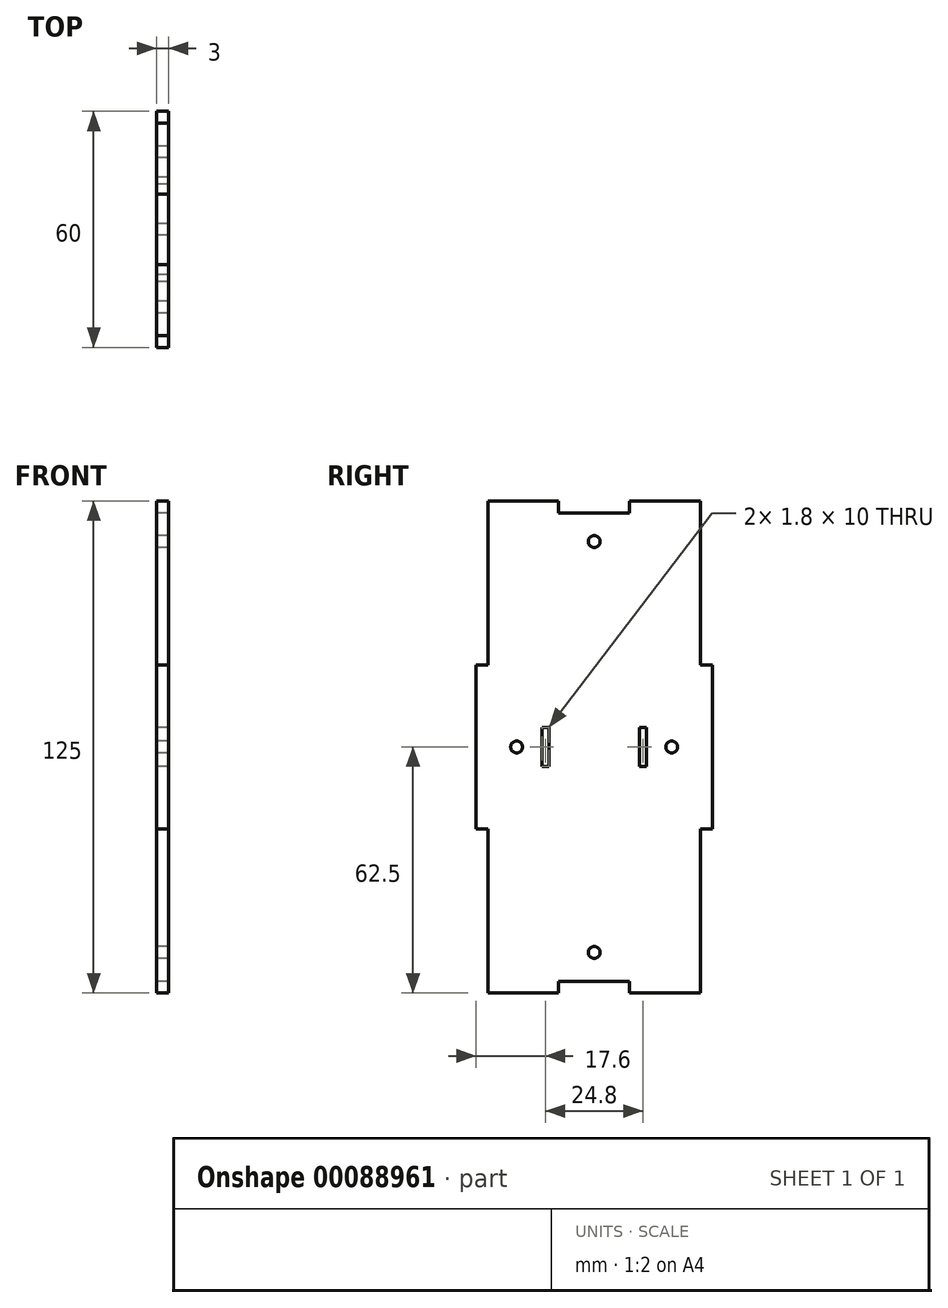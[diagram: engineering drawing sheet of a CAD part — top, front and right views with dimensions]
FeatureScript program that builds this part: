
annotation { "Feature Type Name" : "Feature", "Feature Type Description" : "" }
export const myFeature = defineFeature(function(context is Context, id is Id, definition is map)
    precondition{}
    {
        {
            var Q0;
            Q0=qCreatedBy(makeId("Right.planeOp"),FACE);
            var sketch = newSketch(context, id + "F0", { "sketchPlane" : qUnion([Q0])});
            skLineSegment(sketch, "E0.left", {"start": v(-30, 20.83) * mm, "end": v(-30, -20.83) * mm});
            skLineSegment(sketch, "E1.bottom", {"start": v(-30, 20.83) * mm, "end": v(-27, 20.83) * mm});
            skLineSegment(sketch, "E1.right", {"start": v(-27, 20.83) * mm, "end": v(-27, 62.5) * mm});
            skLineSegment(sketch, "E2.bottom", {"start": v(-30, -20.83) * mm, "end": v(-27, -20.83) * mm});
            skLineSegment(sketch, "E2.right", {"start": v(-27, -20.83) * mm, "end": v(-27, -62.5) * mm});
            skLineSegment(sketch, "E3.left", {"start": v(-9, 62.5) * mm, "end": v(-9, 59.5) * mm});
            skLineSegment(sketch, "E4.left", {"start": v(-9, -62.5) * mm, "end": v(-9, -59.5) * mm});
            skLineSegment(sketch, "E5", {"start": v(-9, 59.5) * mm, "end": v(0, 59.5) * mm});
            skLineSegment(sketch, "E6", {"start": v(0, 59.5) * mm, "end": v(0, 53.7) * mm});
            skLineSegment(sketch, "E7", {"start": v(0, -59.5) * mm, "end": v(-9, -59.5) * mm});
            skLineSegment(sketch, "E8", {"start": v(-27, 62.5) * mm, "end": v(-18, 62.5) * mm});
            skLineSegment(sketch, "E9", {"start": v(-18, 62.5) * mm, "end": v(-9, 62.5) * mm});
            skLineSegment(sketch, "E10", {"start": v(-9, -62.5) * mm, "end": v(-18, -62.5) * mm});
            skLineSegment(sketch, "E11", {"start": v(-18, -62.5) * mm, "end": v(-27, -62.5) * mm});
            skCircle(sketch, "E12", {"center": v(-19.7, 0) * mm, "radius": 1.5 * mm});
            skLineSegment(sketch, "E13.bottom", {"start": v(-13.3, 5) * mm, "end": v(-11.5, 5) * mm});
            skLineSegment(sketch, "E13.top", {"start": v(-13.3, -5) * mm, "end": v(-11.5, -5) * mm});
            skLineSegment(sketch, "E13.left", {"start": v(-13.3, 5) * mm, "end": v(-13.3, -5) * mm});
            skLineSegment(sketch, "E13.right", {"start": v(-11.5, 5) * mm, "end": v(-11.5, -5) * mm});
            skArc(sketch, "E14", {"start": v(0, 53.7) * mm, "mid": v(-1.5, 52.2) * mm, "end": v(0, 50.7) * mm});
            skArc(sketch, "E15.MirrorCS", {"start": v(0, -53.7) * mm, "mid": v(-1.5, -52.2) * mm, "end": v(0, -50.7) * mm});
            skLineSegment(sketch, "E16.trimOffspring", {"start": v(0, 50.7) * mm, "end": v(0, -50.7) * mm});
            skLineSegment(sketch, "E17.trimOffspring", {"start": v(0, -53.7) * mm, "end": v(0, -59.5) * mm});
            skArc(sketch, "E18.MirrorCS", {"start": v(0, 53.7) * mm, "mid": v(1.5, 52.2) * mm, "end": v(0, 50.7) * mm});
            skLineSegment(sketch, "E19.MirrorCS", {"start": v(13.3, 5) * mm, "end": v(11.5, 5) * mm});
            skArc(sketch, "E20.MirrorCS", {"start": v(0, -53.7) * mm, "mid": v(1.5, -52.2) * mm, "end": v(0, -50.7) * mm});
            skLineSegment(sketch, "E21.MirrorCS", {"start": v(30, 20.83) * mm, "end": v(27, 20.83) * mm});
            skLineSegment(sketch, "E22.MirrorCS", {"start": v(9, -62.5) * mm, "end": v(9, -59.5) * mm});
            skLineSegment(sketch, "E23.MirrorCS", {"start": v(9, -62.5) * mm, "end": v(18, -62.5) * mm});
            skLineSegment(sketch, "E24.MirrorCS", {"start": v(30, -20.83) * mm, "end": v(27, -20.83) * mm});
            skLineSegment(sketch, "E25.MirrorCS", {"start": v(13.3, -5) * mm, "end": v(11.5, -5) * mm});
            skLineSegment(sketch, "E26.MirrorCS", {"start": v(18, 62.5) * mm, "end": v(9, 62.5) * mm});
            skLineSegment(sketch, "E27.MirrorCS", {"start": v(9, 62.5) * mm, "end": v(9, 59.5) * mm});
            skLineSegment(sketch, "E28.MirrorCS", {"start": v(11.5, 5) * mm, "end": v(11.5, -5) * mm});
            skLineSegment(sketch, "E29.MirrorCS", {"start": v(9, 59.5) * mm, "end": v(0, 59.5) * mm});
            skCircle(sketch, "E30.MirrorC", {"center": v(19.7, 0) * mm, "radius": 1.5 * mm});
            skLineSegment(sketch, "E31.MirrorCS", {"start": v(30, 20.83) * mm, "end": v(30, -20.83) * mm});
            skLineSegment(sketch, "E32.MirrorCS", {"start": v(27, -20.83) * mm, "end": v(27, -62.5) * mm});
            skLineSegment(sketch, "E33.MirrorCS", {"start": v(13.3, 5) * mm, "end": v(13.3, -5) * mm});
            skLineSegment(sketch, "E34.MirrorCS", {"start": v(0, -59.5) * mm, "end": v(9, -59.5) * mm});
            skLineSegment(sketch, "E35.MirrorCS", {"start": v(27, 62.5) * mm, "end": v(18, 62.5) * mm});
            skLineSegment(sketch, "E36.MirrorCS", {"start": v(27, 20.83) * mm, "end": v(27, 62.5) * mm});
            skLineSegment(sketch, "E37.MirrorCS", {"start": v(18, -62.5) * mm, "end": v(27, -62.5) * mm});
            skSolve(sketch);
        }
        {
            var Q0;
            Q0 = qSketchRegion(id + "F0", true);
            extrude(context, id + "F1", {"entities" : qUnion([Q0]), "depth" : 3 * mm});
        }
    });
